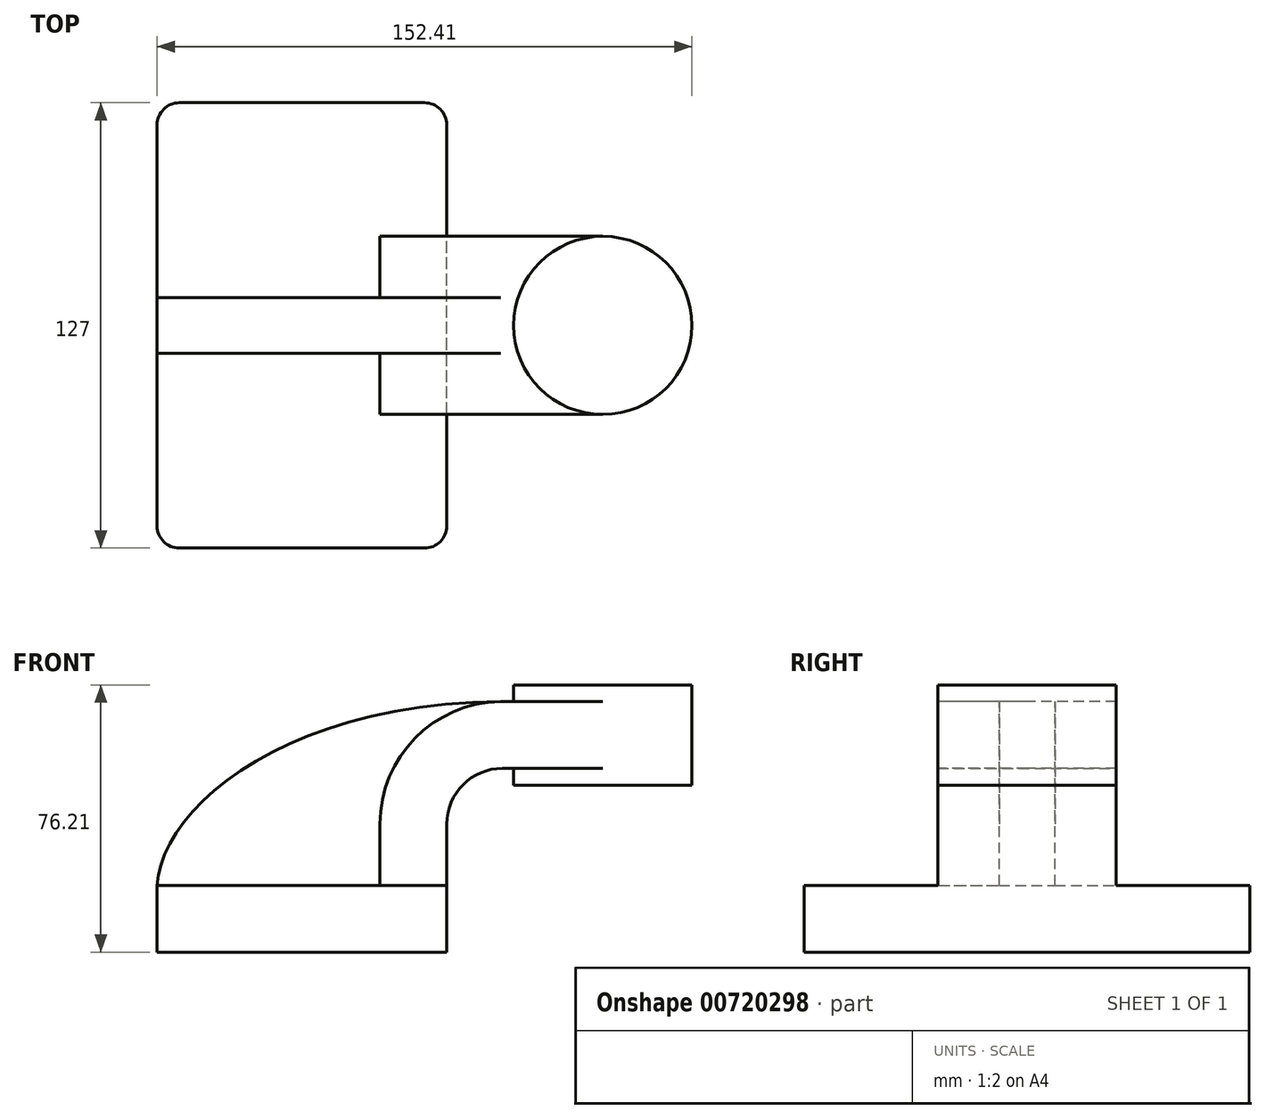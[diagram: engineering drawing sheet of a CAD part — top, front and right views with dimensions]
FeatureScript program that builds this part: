
annotation { "Feature Type Name" : "Feature", "Feature Type Description" : "" }
export const myFeature = defineFeature(function(context is Context, id is Id, definition is map)
    precondition{}
    {
        {
            var Q0;
            Q0=qCreatedBy(makeId("Front.planeOp"),FACE);
            var sketch = newSketch(context, id + "F0", { "sketchPlane" : qUnion([Q0])});
            skLineSegment(sketch, "E0.bottom", {"start": v(41.28, -9.52) * mm, "end": v(-41.28, -9.53) * mm});
            skLineSegment(sketch, "E0.top", {"start": v(41.28, 9.53) * mm, "end": v(-41.28, 9.53) * mm});
            skLineSegment(sketch, "E0.left", {"start": v(41.28, -9.52) * mm, "end": v(41.28, 9.53) * mm});
            skLineSegment(sketch, "E0.right", {"start": v(-41.28, -9.53) * mm, "end": v(-41.28, 9.53) * mm});
            skPoint(sketch, "E0.middle", {"position": v(0, 0) * mm});
            skLineSegment(sketch, "E1.bottom", {"start": v(111.12, 38.1) * mm, "end": v(60.32, 38.1) * mm});
            skLineSegment(sketch, "E1.top", {"start": v(111.12, 66.68) * mm, "end": v(60.32, 66.68) * mm});
            skLineSegment(sketch, "E1.left", {"start": v(111.12, 38.1) * mm, "end": v(111.12, 66.68) * mm});
            skLineSegment(sketch, "E1.right", {"start": v(60.32, 38.1) * mm, "end": v(60.32, 66.68) * mm});
            skPoint(sketch, "E1.middle", {"position": v(85.72, 52.39) * mm});
            skLineSegment(sketch, "E2", {"start": v(41.28, 9.53) * mm, "end": v(41.28, 27) * mm});
            skArc(sketch, "E3", {"start": v(41.27, 27) * mm, "mid": v(45.92, 38.23) * mm, "end": v(57.15, 42.88) * mm});
            skLineSegment(sketch, "E4", {"start": v(57.15, 42.88) * mm, "end": v(85.72, 42.88) * mm});
            skLineSegment(sketch, "E5.0", {"start": v(57.15, 61.93) * mm, "end": v(85.72, 61.93) * mm});
            skArc(sketch, "E5.1", {"start": v(22.23, 27) * mm, "mid": v(32.45, 51.7) * mm, "end": v(57.15, 61.93) * mm});
            skLineSegment(sketch, "E5.2", {"start": v(22.22, 9.53) * mm, "end": v(22.22, 27) * mm});
            skLineSegment(sketch, "E6", {"start": v(85.72, 38.1) * mm, "end": v(85.72, 66.68) * mm});
            skFitSpline(sketch, "E7", {"points": [v(-41.28, 9.52) * mm, v(57.15, 61.93) * mm], "startDerivative": vector(3.99, 64.83) * mm, "endDerivative": vector(189.22, 1.23) * mm});
            skSolve(sketch);
        }
        {
            var Q0;
            Q0=makeQuery(id+"F0.imprint","IMPRINT",FACE,{"disambiguationData":[TD([[makeQuery(id+"F0.imprint","IMPRINT",EDGE,{"derivedFrom":sQuery(id+"F0.wireOp",EDGE,"E0.bottom")}),-1.0]])]});
            extrude(context, id + "F1", {"entities" : qUnion([Q0]), "endBound" : BoundingType.SYMMETRIC, "depth" : 127 * mm, "offsetDistance" : 25.4 * mm});
        }
        {
            var Q0;
            {var subQ1=sQuery(id+"F0.wireOp",EDGE,"E2");Q0=makeQuery(id+"F0.imprint","IMPRINT",FACE,{"disambiguationData":[TD([[makeQuery(id+"F0.imprint","IMPRINT",EDGE,{"derivedFrom":subQ1}),1.0]])]});}
            var Q1;
            {var subQ0=sQuery(id+"F0.wireOp",EDGE,"E4");var subQ1=sQuery(id+"F0.wireOp",EDGE,"E1.right");var subQ2=makeQuery(id+"F0.imprint","INTERSECT",VERTEX,{"derivedFrom":[subQ1,subQ0]});Q1=makeQuery(id+"F0.imprint","IMPRINT",FACE,{"disambiguationData":[TD([[makeQuery(id+"F0.imprint","IMPRINT",EDGE,{"disambiguationData":[TD([[subQ2,-1.0]])],"derivedFrom":subQ1}),-1.0]])]});}
            extrude(context, id + "F2", {"entities" : qUnion([Q0, Q1]), "operationType" : NewBodyOperationType.ADD, "endBound" : BoundingType.SYMMETRIC, "depth" : 50.8 * mm, "offsetDistance" : 25.4 * mm});
        }
        {
            var Q0;
            {var subQ3=sQuery(id+"F0.wireOp",EDGE,"E5.2");Q0=makeQuery(id+"F0.imprint","IMPRINT",FACE,{"disambiguationData":[TD([[makeQuery(id+"F0.imprint","IMPRINT",EDGE,{"derivedFrom":subQ3}),1.0]])]});}
            extrude(context, id + "F3", {"entities" : qUnion([Q0]), "operationType" : NewBodyOperationType.ADD, "endBound" : BoundingType.SYMMETRIC, "depth" : 15.88 * mm, "offsetDistance" : 25.4 * mm});
        }
        {
            var Q0;
            {var subQ0=sQuery(id+"F0.wireOp",EDGE,"E1.left");Q0=makeQuery(id+"F0.imprint","IMPRINT",FACE,{"disambiguationData":[TD([[makeQuery(id+"F0.imprint","IMPRINT",EDGE,{"derivedFrom":subQ0}),1.0]])]});}
            var Q1;
            Q1=sQuery(id+"F0.wireOp",EDGE,"E6");
            revolve(context, id + "F4", {"operationType" : NewBodyOperationType.ADD, "surfaceOperationType" : NewSurfaceOperationType.NEW, "entities" : qUnion([Q0]), "axis" : qUnion([Q1]), "revolveType" : RevolveType.FULL});
        }
        {
            var Q0;
            Q0=makeQuery(id+"F1.opExtrude","CAP_EDGE",EDGE,{"disambiguationData":[OSD([sQuery(id+"F0.wireOp",EDGE,"E0.right")])],"isStart":false});
            var Q1;
            Q1=makeQuery(id+"F1.opExtrude","CAP_EDGE",EDGE,{"disambiguationData":[OSD([sQuery(id+"F0.wireOp",EDGE,"E0.left")])],"isStart":false});
            var Q2;
            Q2=makeQuery(id+"F1.opExtrude","CAP_EDGE",EDGE,{"disambiguationData":[OSD([sQuery(id+"F0.wireOp",EDGE,"E0.left")])],"isStart":true});
            var Q3;
            Q3=makeQuery(id+"F1.opExtrude","CAP_EDGE",EDGE,{"disambiguationData":[OSD([sQuery(id+"F0.wireOp",EDGE,"E0.right")])],"isStart":true});
            fillet(context, id + "F5", {"entities" : qUnion([Q0, Q1, Q2, Q3]), "radius" : 6.35 * mm, "tangentPropagation" : true, "allowEdgeOverflow" : false});
        }
    });
